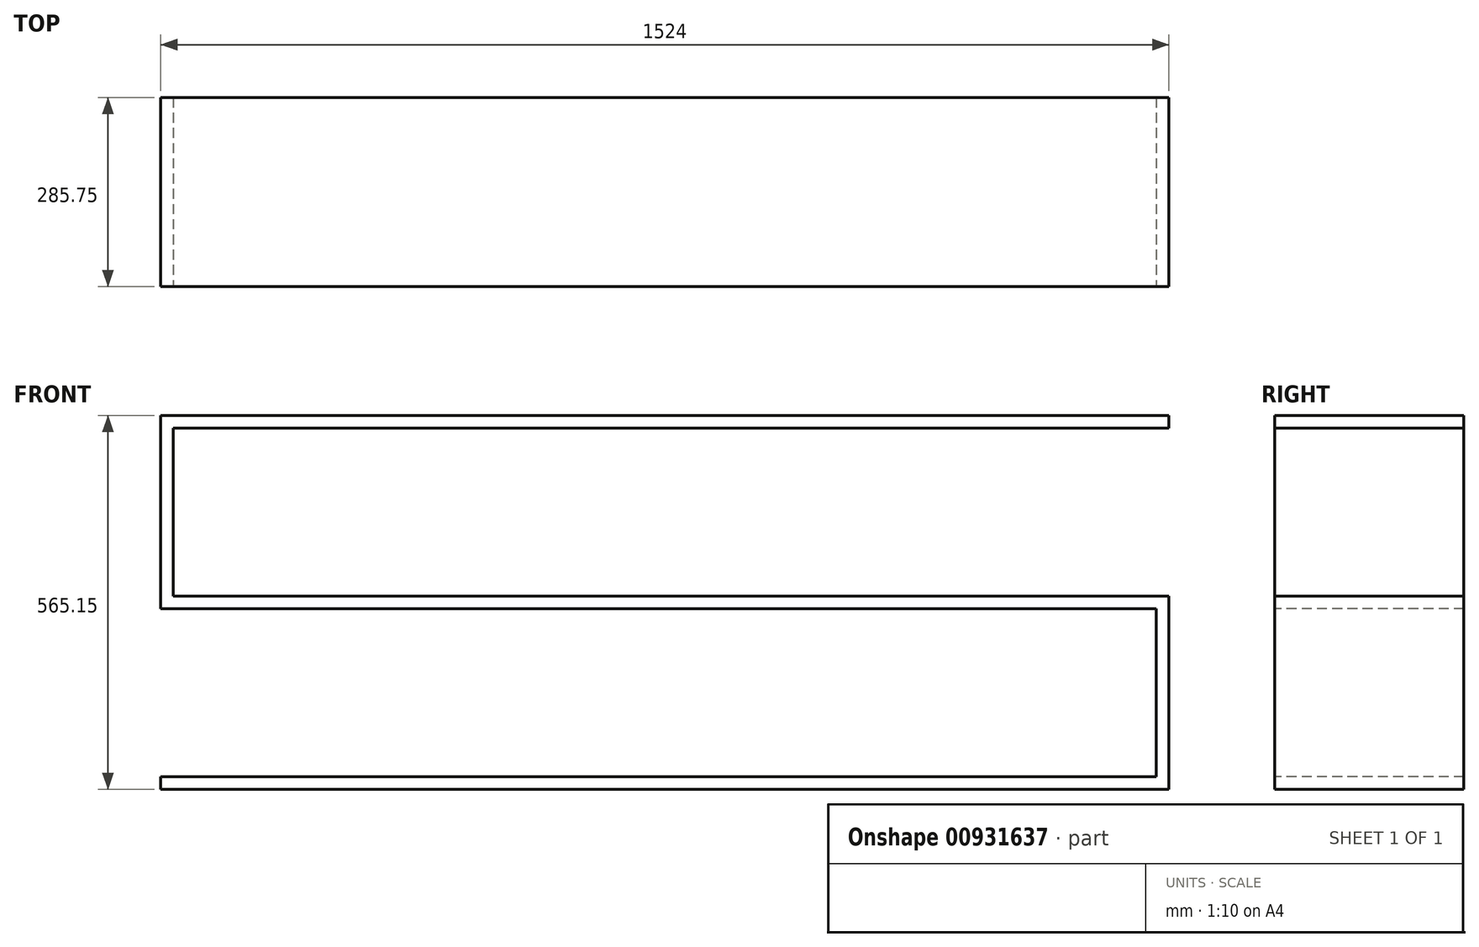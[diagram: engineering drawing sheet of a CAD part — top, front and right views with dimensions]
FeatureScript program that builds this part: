
annotation { "Feature Type Name" : "Feature", "Feature Type Description" : "" }
export const myFeature = defineFeature(function(context is Context, id is Id, definition is map)
    precondition{}
    {
        {
            var Q0;
            Q0=qCreatedBy(makeId("Top.planeOp"),FACE);
            var sketch = newSketch(context, id + "F0", { "sketchPlane" : qUnion([Q0])});
            skLineSegment(sketch, "E0.bottom", {"start": v(-575.43, -221.99) * mm, "end": v(948.57, -221.99) * mm});
            skLineSegment(sketch, "E0.top", {"start": v(-575.43, 63.76) * mm, "end": v(948.57, 63.76) * mm});
            skLineSegment(sketch, "E0.left", {"start": v(-575.43, -221.99) * mm, "end": v(-575.43, 63.76) * mm});
            skLineSegment(sketch, "E0.right", {"start": v(948.57, -221.99) * mm, "end": v(948.57, 63.76) * mm});
            skSolve(sketch);
        }
        {
            var Q0;
            Q0=makeQuery(id+"F0.imprint","IMPRINT",FACE,{"disambiguationData":[TD([[makeQuery(id+"F0.imprint","IMPRINT",EDGE,{"derivedFrom":sQuery(id+"F0.wireOp",EDGE,"E0.bottom")}),1.0]])]});
            extrude(context, id + "F1", {"entities" : qUnion([Q0]), "depth" : 19.05 * mm, "offsetDistance" : 25.4 * mm});
        }
        {
            var Q0;
            Q0=makeQuery(id+"F1.opExtrude","CAP_FACE",FACE,{"disambiguationData":[OSD([sQuery(id+"F0.wireOp",EDGE,"E0.bottom"),sQuery(id+"F0.wireOp",EDGE,"E0.top"),sQuery(id+"F0.wireOp",EDGE,"E0.left"),sQuery(id+"F0.wireOp",EDGE,"E0.right")])],"isStart":true});
            var sketch = newSketch(context, id + "F2", { "sketchPlane" : qUnion([Q0])});
            skLineSegment(sketch, "E1", {"start": v(-575.43, 221.99) * mm, "end": v(-575.43, -63.76) * mm});
            skLineSegment(sketch, "E2", {"start": v(-575.43, -63.76) * mm, "end": v(-556.38, -63.76) * mm});
            skLineSegment(sketch, "E3", {"start": v(-556.38, -63.76) * mm, "end": v(-556.38, 221.99) * mm});
            skLineSegment(sketch, "E4", {"start": v(-556.38, 221.99) * mm, "end": v(-575.43, 221.99) * mm});
            skSolve(sketch);
        }
        {
            var Q0;
            Q0=makeQuery(id+"F2.imprint","IMPRINT",FACE,{"disambiguationData":[TD([[makeQuery(id+"F2.imprint","IMPRINT",EDGE,{"derivedFrom":sQuery(id+"F2.wireOp",EDGE,"E1")}),1.0]])]});
            extrude(context, id + "F3", {"entities" : qUnion([Q0]), "operationType" : NewBodyOperationType.ADD, "depth" : 254 * mm, "offsetDistance" : 25.4 * mm});
        }
        {
            var Q0;
            Q0=makeQuery(id+"F3.opExtrude","CAP_FACE",FACE,{"disambiguationData":[OSD([sQuery(id+"F2.wireOp",EDGE,"E1"),sQuery(id+"F2.wireOp",EDGE,"E2"),sQuery(id+"F2.wireOp",EDGE,"E3"),sQuery(id+"F2.wireOp",EDGE,"E4")])],"isStart":false});
            var sketch = newSketch(context, id + "F4", { "sketchPlane" : qUnion([Q0])});
            skLineSegment(sketch, "E5", {"start": v(-575.43, 221.99) * mm, "end": v(-575.43, -63.76) * mm});
            skLineSegment(sketch, "E6", {"start": v(-575.43, -63.76) * mm, "end": v(948.57, -63.76) * mm});
            skLineSegment(sketch, "E7", {"start": v(948.57, -63.76) * mm, "end": v(948.57, 221.99) * mm});
            skLineSegment(sketch, "E8", {"start": v(948.57, 221.99) * mm, "end": v(-575.43, 221.99) * mm});
            skSolve(sketch);
        }
        {
            var Q0;
            {var subQ2=sQuery(id+"F4.wireOp",EDGE,"E7");Q0=makeQuery(id+"F4.imprint","IMPRINT",FACE,{"disambiguationData":[TD([[makeQuery(id+"F4.imprint","IMPRINT",EDGE,{"derivedFrom":subQ2}),1.0]])]});}
            var Q1;
            {var subQ0=sQuery(id+"F4.wireOp",EDGE,"E5");Q1=makeQuery(id+"F4.imprint","IMPRINT",FACE,{"disambiguationData":[TD([[makeQuery(id+"F4.imprint","IMPRINT",EDGE,{"derivedFrom":subQ0}),1.0]])]});}
            extrude(context, id + "F5", {"entities" : qUnion([Q0, Q1]), "operationType" : NewBodyOperationType.ADD, "depth" : 19.05 * mm, "offsetDistance" : 25.4 * mm});
        }
        {
            var Q0;
            Q0=makeQuery(id+"F5.opExtrude","CAP_FACE",FACE,{"disambiguationData":[OSD([sQuery(id+"F4.wireOp",EDGE,"E5"),sQuery(id+"F4.wireOp",EDGE,"E6"),sQuery(id+"F4.wireOp",EDGE,"E7"),sQuery(id+"F4.wireOp",EDGE,"E8")])],"isStart":false});
            var sketch = newSketch(context, id + "F6", { "sketchPlane" : qUnion([Q0])});
            skLineSegment(sketch, "E9", {"start": v(948.57, 221.99) * mm, "end": v(948.57, -63.76) * mm});
            skLineSegment(sketch, "E10", {"start": v(948.57, -63.76) * mm, "end": v(929.52, -63.76) * mm});
            skLineSegment(sketch, "E11", {"start": v(929.52, -63.76) * mm, "end": v(929.52, 221.99) * mm});
            skLineSegment(sketch, "E12", {"start": v(929.52, 221.99) * mm, "end": v(948.57, 221.99) * mm});
            skSolve(sketch);
        }
        {
            var Q0;
            Q0=makeQuery(id+"F6.imprint","IMPRINT",FACE,{"disambiguationData":[TD([[makeQuery(id+"F6.imprint","IMPRINT",EDGE,{"derivedFrom":sQuery(id+"F6.wireOp",EDGE,"E9")}),1.0]])]});
            extrude(context, id + "F7", {"entities" : qUnion([Q0]), "operationType" : NewBodyOperationType.ADD, "depth" : 254 * mm, "offsetDistance" : 25.4 * mm});
        }
        {
            var Q0;
            Q0=makeQuery(id+"F7.opExtrude","CAP_FACE",FACE,{"disambiguationData":[OSD([sQuery(id+"F6.wireOp",EDGE,"E9"),sQuery(id+"F6.wireOp",EDGE,"E10"),sQuery(id+"F6.wireOp",EDGE,"E11"),sQuery(id+"F6.wireOp",EDGE,"E12")])],"isStart":false});
            var sketch = newSketch(context, id + "F8", { "sketchPlane" : qUnion([Q0])});
            skLineSegment(sketch, "E13", {"start": v(948.57, 221.99) * mm, "end": v(948.57, -63.76) * mm});
            skLineSegment(sketch, "E14", {"start": v(948.57, -63.76) * mm, "end": v(-575.43, -63.76) * mm});
            skLineSegment(sketch, "E15", {"start": v(-575.43, -63.76) * mm, "end": v(-575.43, 221.99) * mm});
            skLineSegment(sketch, "E16", {"start": v(-575.43, 221.99) * mm, "end": v(948.57, 221.99) * mm});
            skSolve(sketch);
        }
        {
            var Q0;
            {var subQ2=sQuery(id+"F8.wireOp",EDGE,"E15");Q0=makeQuery(id+"F8.imprint","IMPRINT",FACE,{"disambiguationData":[TD([[makeQuery(id+"F8.imprint","IMPRINT",EDGE,{"derivedFrom":subQ2}),-1.0]])]});}
            var Q1;
            {var subQ0=sQuery(id+"F8.wireOp",EDGE,"E13");Q1=makeQuery(id+"F8.imprint","IMPRINT",FACE,{"disambiguationData":[TD([[makeQuery(id+"F8.imprint","IMPRINT",EDGE,{"derivedFrom":subQ0}),1.0]])]});}
            extrude(context, id + "F9", {"entities" : qUnion([Q0, Q1]), "operationType" : NewBodyOperationType.ADD, "depth" : 19.05 * mm, "offsetDistance" : 25.4 * mm});
        }
    });
